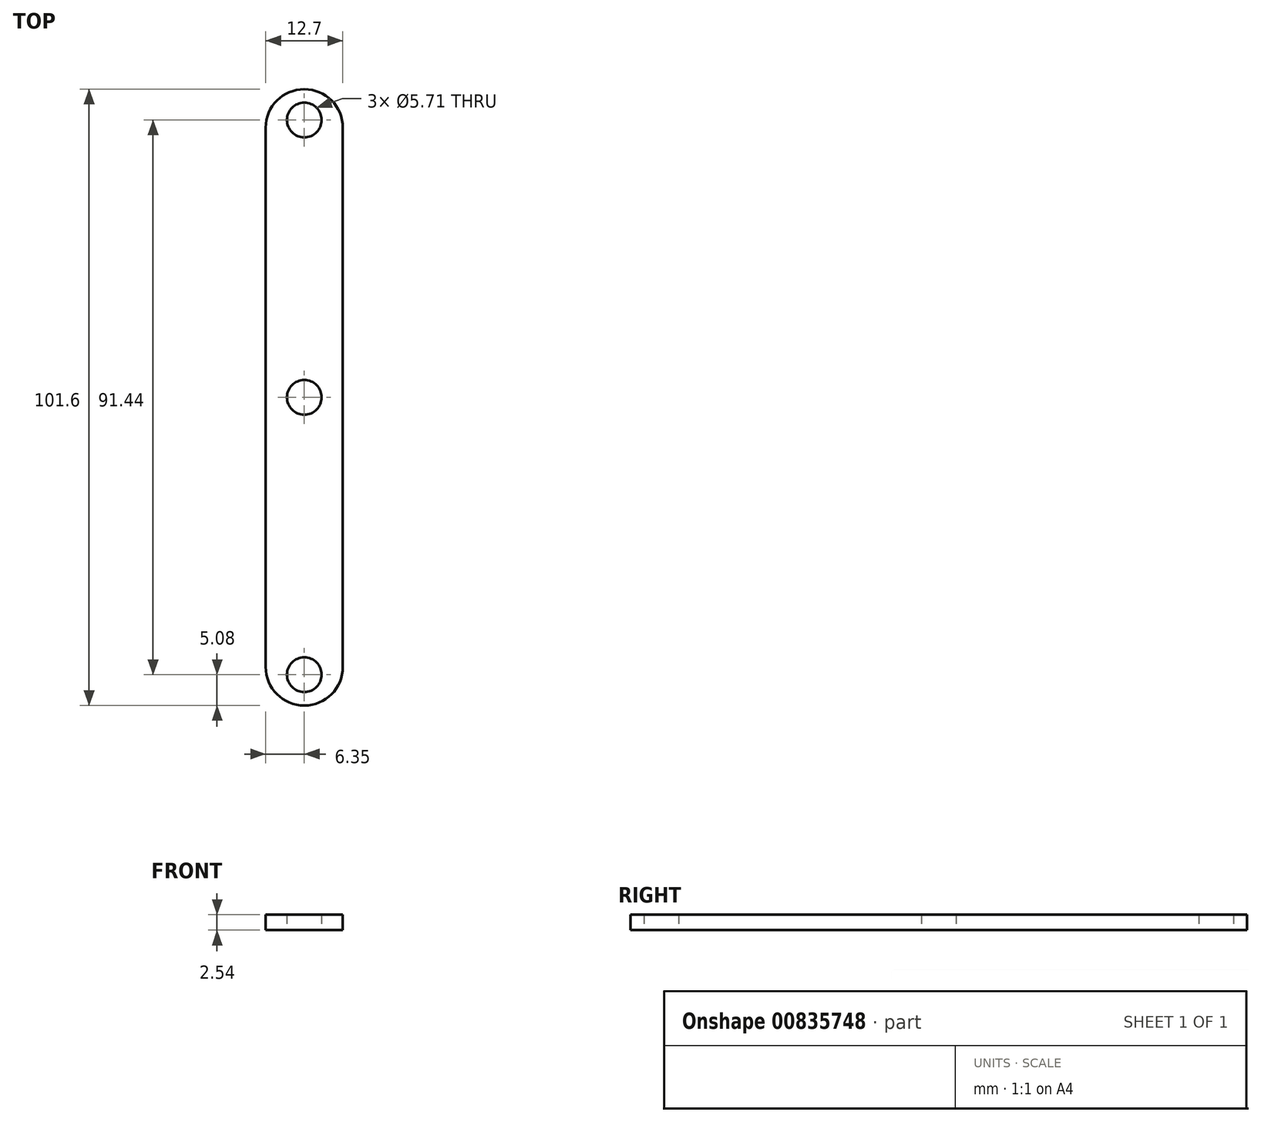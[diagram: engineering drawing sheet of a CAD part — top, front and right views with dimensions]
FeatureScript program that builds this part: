
annotation { "Feature Type Name" : "Feature", "Feature Type Description" : "" }
export const myFeature = defineFeature(function(context is Context, id is Id, definition is map)
    precondition{}
    {
        {
            var Q0;
            Q0=qCreatedBy(makeId("Top.planeOp"),FACE);
            var sketch = newSketch(context, id + "F0", { "sketchPlane" : qUnion([Q0])});
            skLineSegment(sketch, "E0.bottom", {"start": v(-6.35, 50.8) * mm, "end": v(6.35, 50.8) * mm});
            skLineSegment(sketch, "E0.top", {"start": v(-6.35, -50.8) * mm, "end": v(6.35, -50.8) * mm});
            skLineSegment(sketch, "E0.left", {"start": v(-6.35, 50.8) * mm, "end": v(-6.35, -50.8) * mm});
            skLineSegment(sketch, "E0.right", {"start": v(6.35, 50.8) * mm, "end": v(6.35, -50.8) * mm});
            skPoint(sketch, "E0.middle", {"position": v(0, 0) * mm});
            skCircle(sketch, "E1", {"center": v(0, 0) * mm, "radius": 2.86 * mm});
            skCircle(sketch, "E2", {"center": v(0, -45.72) * mm, "radius": 2.86 * mm});
            skCircle(sketch, "E3.MirrorC", {"center": v(0, 45.72) * mm, "radius": 2.86 * mm});
            skSolve(sketch);
        }
        {
            var Q0;
            Q0=makeQuery(id+"F0.imprint","IMPRINT",FACE,{"disambiguationData":[TD([[makeQuery(id+"F0.imprint","IMPRINT",EDGE,{"derivedFrom":sQuery(id+"F0.wireOp",EDGE,"E0.bottom")}),-1.0]])]});
            extrude(context, id + "F1", {"entities" : qUnion([Q0]), "depth" : 2.54 * mm, "offsetDistance" : 25.4 * mm});
        }
        {
            var Q0;
            Q0=makeQuery(id+"F1.opExtrude","SWEPT_EDGE",EDGE,{"disambiguationData":[OSD([sQuery(id+"F0.wireOp",EDGE,"E0.top"),sQuery(id+"F0.wireOp",EDGE,"E0.right")])]});
            var Q1;
            Q1=makeQuery(id+"F1.opExtrude","SWEPT_EDGE",EDGE,{"disambiguationData":[OSD([sQuery(id+"F0.wireOp",EDGE,"E0.top"),sQuery(id+"F0.wireOp",EDGE,"E0.left")])]});
            var Q2;
            Q2=makeQuery(id+"F1.opExtrude","SWEPT_EDGE",EDGE,{"disambiguationData":[OSD([sQuery(id+"F0.wireOp",EDGE,"E0.bottom"),sQuery(id+"F0.wireOp",EDGE,"E0.right")])]});
            var Q3;
            Q3=makeQuery(id+"F1.opExtrude","SWEPT_EDGE",EDGE,{"disambiguationData":[OSD([sQuery(id+"F0.wireOp",EDGE,"E0.bottom"),sQuery(id+"F0.wireOp",EDGE,"E0.left")])]});
            fillet(context, id + "F2", {"entities" : qUnion([Q0, Q1, Q2, Q3]), "radius" : 6.35 * mm, "tangentPropagation" : true, "allowEdgeOverflow" : false});
        }
    });
